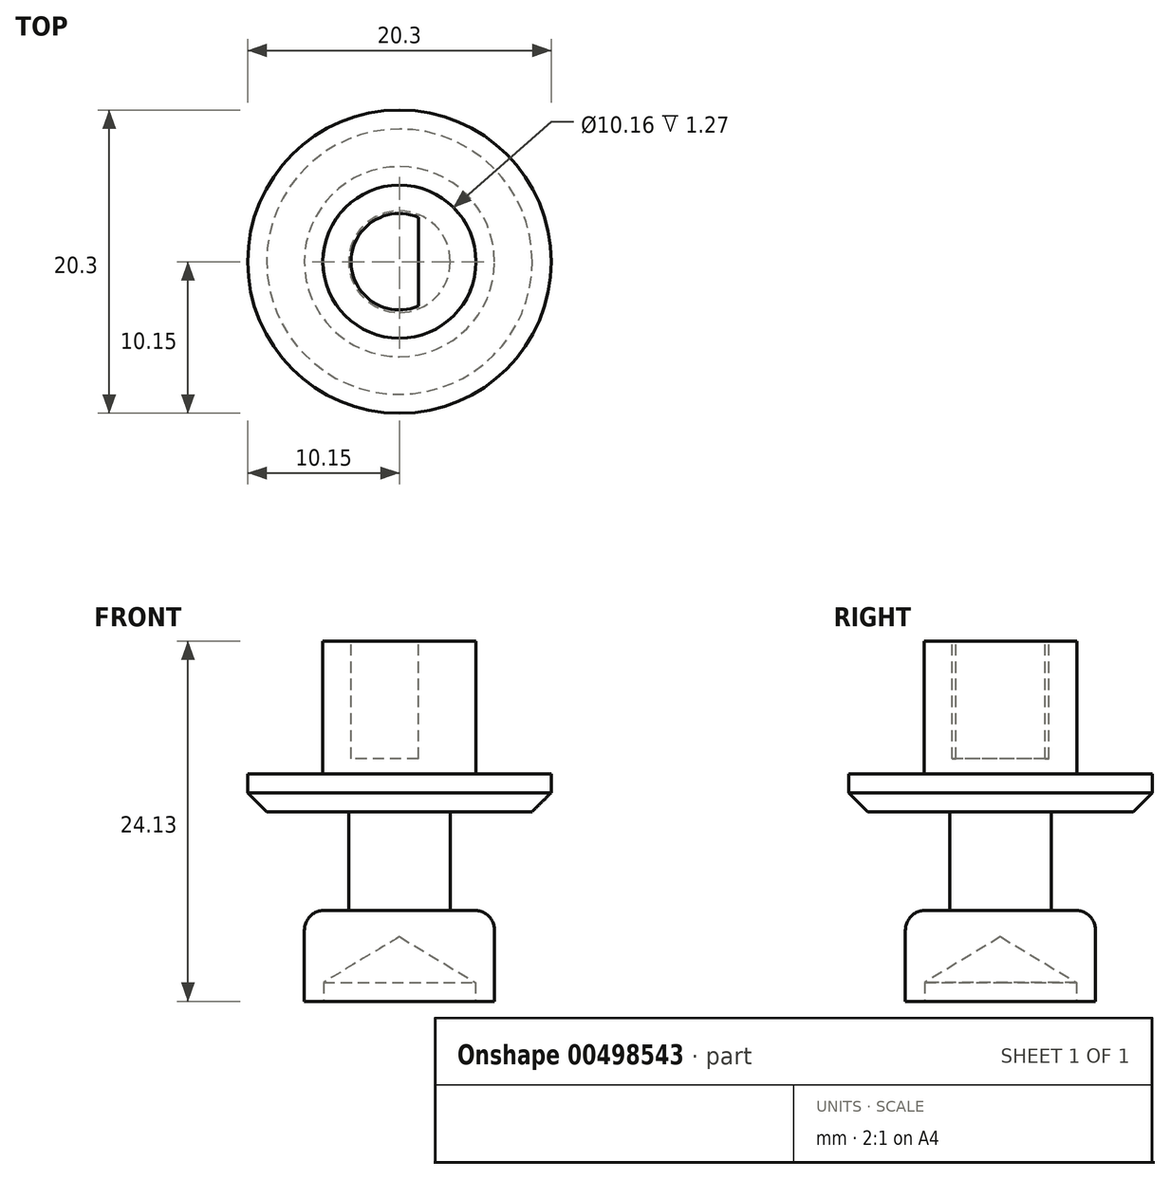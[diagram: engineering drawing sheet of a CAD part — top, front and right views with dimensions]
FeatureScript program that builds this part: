
annotation { "Feature Type Name" : "Feature", "Feature Type Description" : "" }
export const myFeature = defineFeature(function(context is Context, id is Id, definition is map)
    precondition{}
    {
        {
            var Q0;
            Q0=qCreatedBy(makeId("Top.planeOp"),FACE);
            var sketch = newSketch(context, id + "F0", { "sketchPlane" : qUnion([Q0])});
            skCircle(sketch, "E0", {"center": v(0, 0) * mm, "radius": 6.36 * mm});
            skSolve(sketch);
        }
        {
            var Q0;
            Q0 = qSketchRegion(id + "F0", true);
            extrude(context, id + "F1", {"entities" : qUnion([Q0]), "depth" : 6.1 * mm});
        }
        {
            var Q0;
            Q0=qCreatedBy(makeId("Top.planeOp"),FACE);
            var sketch = newSketch(context, id + "F2", { "sketchPlane" : qUnion([Q0])});
            skCircle(sketch, "E1", {"center": v(0, 0) * mm, "radius": 3.4 * mm});
            skSolve(sketch);
        }
        {
            var Q0;
            Q0 = qSketchRegion(id + "F2", true);
            extrude(context, id + "F3", {"entities" : qUnion([Q0]), "operationType" : NewBodyOperationType.ADD, "depth" : 12.7 * mm});
        }
        {
            var Q0;
            Q0=makeQuery(id+"F3.opExtrude","CAP_FACE",FACE,{"disambiguationData":[OSD([sQuery(id+"F2.wireOp",EDGE,"E1")])],"isStart":false});
            cPlane(context, id + "F4", {"entities" : qUnion([Q0]), "cplaneType" : CPlaneType.OFFSET, "offset" : 0 * mm, "width" : 152.4 * mm, "height" : 152.4 * mm});
        }
        {
            var Q0;
            Q0=qCreatedBy(id+"F4.planeOp",FACE);
            var sketch = newSketch(context, id + "F5", { "sketchPlane" : qUnion([Q0])});
            skCircle(sketch, "E2", {"center": v(0, 0) * mm, "radius": 10.15 * mm});
            skSolve(sketch);
        }
        {
            var Q0;
            Q0 = qSketchRegion(id + "F5", true);
            extrude(context, id + "F6", {"entities" : qUnion([Q0]), "operationType" : NewBodyOperationType.ADD, "depth" : 2.54 * mm});
        }
        {
            var Q0;
            Q0=makeQuery(id+"F6.opExtrude","CAP_FACE",FACE,{"disambiguationData":[OSD([sQuery(id+"F5.wireOp",EDGE,"E2")])],"isStart":false});
            cPlane(context, id + "F7", {"entities" : qUnion([Q0]), "cplaneType" : CPlaneType.OFFSET, "offset" : 0 * mm, "width" : 152.4 * mm, "height" : 152.4 * mm});
        }
        {
            var Q0;
            Q0=qCreatedBy(id+"F7.planeOp",FACE);
            var sketch = newSketch(context, id + "F8", { "sketchPlane" : qUnion([Q0])});
            skCircle(sketch, "E3", {"center": v(0, 0) * mm, "radius": 5.12 * mm});
            skSolve(sketch);
        }
        {
            var Q0;
            Q0 = qSketchRegion(id + "F8", true);
            extrude(context, id + "F9", {"entities" : qUnion([Q0]), "depth" : 8.9 * mm});
        }
        {
            var Q0;
            Q0=makeQuery(id+"F9.opExtrude","CAP_FACE",FACE,{"disambiguationData":[OSD([sQuery(id+"F8.wireOp",EDGE,"E3")])],"isStart":false});
            cPlane(context, id + "F10", {"entities" : qUnion([Q0]), "cplaneType" : CPlaneType.OFFSET, "offset" : 0 * mm, "width" : 152.4 * mm, "height" : 152.4 * mm});
        }
        {
            var Q0;
            Q0=qCreatedBy(id+"F10.planeOp",FACE);
            var sketch = newSketch(context, id + "F11", { "sketchPlane" : qUnion([Q0])});
            skCircle(sketch, "E4", {"center": v(0, 0) * mm, "radius": 3.23 * mm});
            skLineSegment(sketch, "E5", {"start": v(1.26, 0) * mm, "end": v(1.26, 2.98) * mm});
            skLineSegment(sketch, "E6", {"start": v(1.26, 2.98) * mm, "end": v(1.26, -2.98) * mm});
            skSolve(sketch);
        }
        {
            var Q0;
            {var subQ0=sQuery(id+"F11.wireOp",EDGE,"E6");var subQ4=makeQuery(id+"F11.imprint","IMPRINT",VERTEX,{"derivedFrom":subQ0});Q0=makeQuery(id+"F11.imprint","IMPRINT",FACE,{"disambiguationData":[TD([[makeQuery(id+"F11.imprint","IMPRINT",EDGE,{"disambiguationData":[TD([[subQ4,1.0]])],"derivedFrom":subQ0}),-1.0]])]});}
            extrude(context, id + "F12", {"entities" : qUnion([Q0]), "operationType" : NewBodyOperationType.REMOVE, "oppositeDirection" : true, "depth" : 7.87 * mm});
        }
        {
            var Q0;
            Q0=sQuery(id+"F0.wireOp",VERTEX,"E0.center");
            var Q1;
            Q1=makeQuery(id+"F1.opExtrude","SWEPT_BODY",BODY,{"disambiguationData":[OSD([sQuery(id+"F0.wireOp",EDGE,"E0")])]});
            hole(context, id + "F13", {"style" : HoleStyle.SIMPLE, "endStyle" : HoleEndStyle.BLIND, "oppositeDirection" : true, "holeDiameter" : 10.16 * mm, "holeDepth" : 1.27 * mm, "isTappedThrough" : true, "tappedDepth" : 12.7 * mm, "tapClearance" : 3, "locations" : qUnion([Q0]), "scope" : qUnion([Q1])});
        }
        {
            var Q0;
            Q0=makeQuery(id+"F1.opExtrude","CAP_EDGE",EDGE,{"disambiguationData":[OSD([sQuery(id+"F0.wireOp",EDGE,"E0")])],"isStart":false});
            fillet(context, id + "F14", {"entities" : qUnion([Q0]), "radius" : 1.35 * mm, "tangentPropagation" : true, "allowEdgeOverflow" : false});
        }
        {
            var Q0;
            Q0=makeQuery(id+"F6.opExtrude","CAP_EDGE",EDGE,{"disambiguationData":[OSD([sQuery(id+"F5.wireOp",EDGE,"E2")])],"isStart":true});
            chamfer(context, id + "F15", {"entities" : qUnion([Q0]), "width" : 1.27 * mm, "tangentPropagation" : true});
        }
    });
